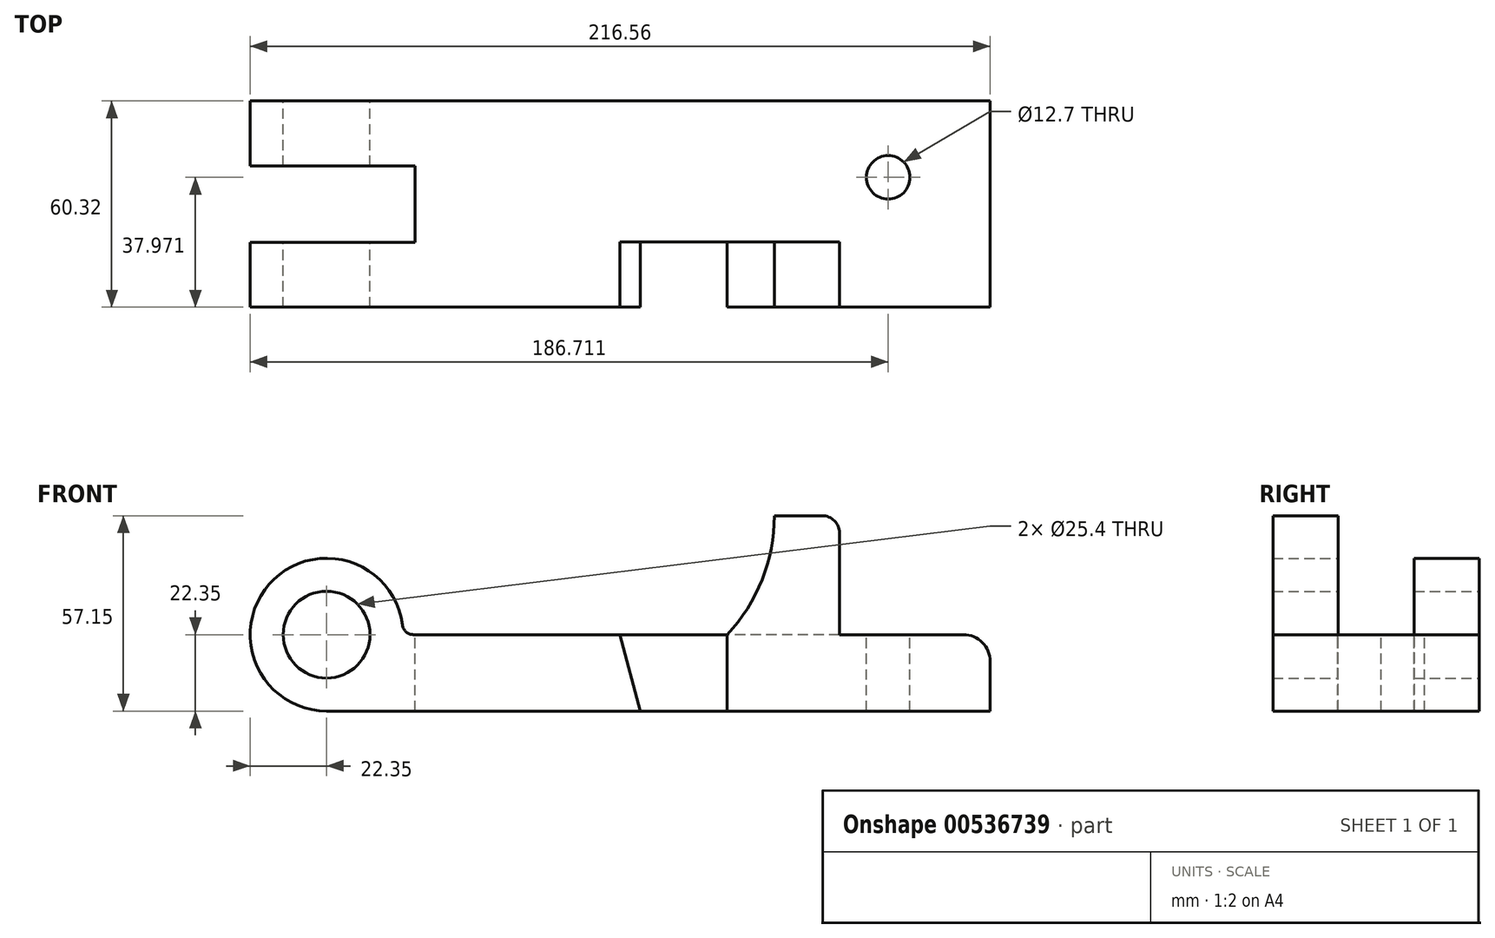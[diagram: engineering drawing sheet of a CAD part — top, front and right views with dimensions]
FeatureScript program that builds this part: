
annotation { "Feature Type Name" : "Feature", "Feature Type Description" : "" }
export const myFeature = defineFeature(function(context is Context, id is Id, definition is map)
    precondition{}
    {
        {
            var Q0;
            Q0=qCreatedBy(makeId("Front.planeOp"),FACE);
            var sketch = newSketch(context, id + "F0", { "sketchPlane" : qUnion([Q0])});
            skCircle(sketch, "E0", {"center": v(0, 0) * mm, "radius": 12.7 * mm});
            skCircle(sketch, "E1", {"center": v(0, 0) * mm, "radius": 22.35 * mm});
            skLineSegment(sketch, "E2.bottom", {"start": v(0, -22.35) * mm, "end": v(194.2, -22.35) * mm});
            skLineSegment(sketch, "E2.top", {"start": v(22.35, 0) * mm, "end": v(194.2, 0) * mm});
            skLineSegment(sketch, "E2.right", {"start": v(194.2, -22.35) * mm, "end": v(194.2, 0) * mm});
            skSolve(sketch);
        }
        {
            var Q0;
            {var subQ0=sQuery(id+"F0.wireOp",EDGE,"E2.bottom");Q0=makeQuery(id+"F0.imprint","IMPRINT",FACE,{"disambiguationData":[TD([[makeQuery(id+"F0.imprint","IMPRINT",EDGE,{"derivedFrom":subQ0}),1.0]])]});}
            var Q1;
            Q1=makeQuery(id+"F0.imprint","IMPRINT",FACE,{"disambiguationData":[TD([[makeQuery(id+"F0.imprint","IMPRINT",EDGE,{"derivedFrom":sQuery(id+"F0.wireOp",EDGE,"E0")}),-1.0]])]});
            extrude(context, id + "F1", {"entities" : qUnion([Q0, Q1]), "endBound" : BoundingType.SYMMETRIC, "depth" : 60.32 * mm, "offsetDistance" : 25.4 * mm});
        }
        {
            var Q0;
            Q0=qCreatedBy(makeId("Top.planeOp"),FACE);
            var sketch = newSketch(context, id + "F2", { "sketchPlane" : qUnion([Q0])});
            skLineSegment(sketch, "E3", {"start": v(-22.35, -30.16) * mm, "end": v(-22.35, 30.16) * mm});
            skLineSegment(sketch, "E4.bottom", {"start": v(-22.35, 11.16) * mm, "end": v(25.9, 11.16) * mm});
            skLineSegment(sketch, "E4.top", {"start": v(-22.35, -11.16) * mm, "end": v(25.9, -11.16) * mm});
            skLineSegment(sketch, "E4.left", {"start": v(-22.35, 11.16) * mm, "end": v(-22.35, -11.16) * mm});
            skLineSegment(sketch, "E4.right", {"start": v(25.9, 11.16) * mm, "end": v(25.9, -11.16) * mm});
            skPoint(sketch, "E4.middle", {"position": v(1.78, 0) * mm});
            skSolve(sketch);
        }
        {
            var Q0;
            Q0=makeQuery(id+"F2.imprint","IMPRINT",FACE,{"disambiguationData":[TD([[makeQuery(id+"F2.imprint","IMPRINT",EDGE,{"derivedFrom":sQuery(id+"F2.wireOp",EDGE,"E4.bottom")}),-1.0]])]});
            extrude(context, id + "F3", {"entities" : qUnion([Q0]), "operationType" : NewBodyOperationType.REMOVE, "endBound" : BoundingType.SYMMETRIC, "oppositeDirection" : true, "depth" : .88 * 50.8 * mm, "offsetDistance" : 25.4 * mm});
        }
        {
            var Q0;
            Q0=makeQuery(id+"F1.opExtrude","CAP_FACE",FACE,{"disambiguationData":[OSD([sQuery(id+"F0.wireOp",EDGE,"E0"),sQuery(id+"F0.wireOp",EDGE,"E1"),sQuery(id+"F0.wireOp",EDGE,"E2.bottom"),sQuery(id+"F0.wireOp",EDGE,"E2.top"),sQuery(id+"F0.wireOp",EDGE,"E2.right")])],"isStart":false});
            var sketch = newSketch(context, id + "F4", { "sketchPlane" : qUnion([Q0])});
            skLineSegment(sketch, "E5", {"start": v(91.85, -22.35) * mm, "end": v(117.25, -22.35) * mm});
            skLineSegment(sketch, "E6", {"start": v(117.25, -22.35) * mm, "end": v(117.25, 0) * mm});
            skLineSegment(sketch, "E7", {"start": v(117.25, 0) * mm, "end": v(85.85, 0) * mm});
            skLineSegment(sketch, "E8", {"start": v(85.85, 0) * mm, "end": v(91.85, -22.35) * mm});
            skSolve(sketch);
        }
        {
            var Q0;
            Q0=makeQuery(id+"F4.imprint","IMPRINT",FACE,{"disambiguationData":[TD([[makeQuery(id+"F4.imprint","IMPRINT",EDGE,{"derivedFrom":sQuery(id+"F4.wireOp",EDGE,"E5")}),1.0]])]});
            extrude(context, id + "F5", {"entities" : qUnion([Q0]), "operationType" : NewBodyOperationType.REMOVE, "oppositeDirection" : true, "depth" : 19.05 * mm, "offsetDistance" : 25.4 * mm});
        }
        {
            var Q0;
            {var subQ0=sQuery(id+"F0.wireOp",EDGE,"E2.bottom");var subQ1=sQuery(id+"F0.wireOp",EDGE,"E2.top");var subQ2=sQuery(id+"F0.wireOp",EDGE,"E2.right");Q0=makeQuery(id+"F5.boolean.opBoolean","SPLIT",FACE,{"disambiguationData":[TD([makeQuery(id+"F1.opExtrude","SWEPT_FACE",FACE,{"disambiguationData":[OSD([subQ2])]})])],"derivedFrom":makeQuery(id+"F1.opExtrude","CAP_FACE",FACE,{"disambiguationData":[OSD([sQuery(id+"F0.wireOp",EDGE,"E0"),sQuery(id+"F0.wireOp",EDGE,"E1"),subQ0,subQ1,subQ2])],"isStart":false})});}
            var sketch = newSketch(context, id + "F6", { "sketchPlane" : qUnion([Q0])});
            skLineSegment(sketch, "E9", {"start": v(150.09, 0) * mm, "end": v(150.09, 34.8) * mm});
            skLineSegment(sketch, "E10", {"start": v(150.09, 34.8) * mm, "end": v(131.04, 34.8) * mm});
            skArc(sketch, "E11", {"start": v(117.25, 0) * mm, "mid": v(127.46, 16.08) * mm, "end": v(131.04, 34.8) * mm});
            skSolve(sketch);
        }
        {
            var Q0;
            Q0 = qSketchRegion(id + "F6", true);
            var Q1;
            {var subQ0=sQuery(id+"F6.wireOp",EDGE,"E9");Q1=makeQuery(id+"F6.imprint","IMPRINT",FACE,{"disambiguationData":[TD([[makeQuery(id+"F6.imprint","IMPRINT",EDGE,{"derivedFrom":subQ0}),1.0]])]});}
            var Q2;
            Q2=makeQuery(id+"F5.boolean.opBoolean","COPY",FACE,{"derivedFrom":makeQuery(id+"F5.opExtrude","CAP_FACE",FACE,{"disambiguationData":[OSD([sQuery(id+"F4.wireOp",EDGE,"E5"),sQuery(id+"F4.wireOp",EDGE,"E6"),sQuery(id+"F4.wireOp",EDGE,"E7"),sQuery(id+"F4.wireOp",EDGE,"E8")])],"isStart":false})});
            extrude(context, id + "F7", {"entities" : qUnion([Q0, Q1]), "operationType" : NewBodyOperationType.ADD, "endBound" : BoundingType.UP_TO_SURFACE, "oppositeDirection" : true, "depth" : 25.4 * mm, "endBoundEntityFace" : qUnion([Q2]), "offsetDistance" : 25.4 * mm});
        }
        {
            var Q0;
            Q0=makeQuery(id+"F1.opExtrude","SWEPT_FACE",FACE,{"disambiguationData":[OSD([sQuery(id+"F0.wireOp",EDGE,"E2.top")])]});
            var sketch = newSketch(context, id + "F8", { "sketchPlane" : qUnion([Q0])});
            skCircle(sketch, "E12", {"center": v(164.36, 7.81) * mm, "radius": 6.35 * mm});
            skSolve(sketch);
        }
        {
            var Q0;
            Q0=makeQuery(id+"F8.imprint","IMPRINT",FACE,{"disambiguationData":[TD([[makeQuery(id+"F8.imprint","IMPRINT",EDGE,{"derivedFrom":sQuery(id+"F8.wireOp",EDGE,"E12")}),1.0]])]});
            extrude(context, id + "F9", {"entities" : qUnion([Q0]), "operationType" : NewBodyOperationType.REMOVE, "endBound" : BoundingType.THROUGH_ALL, "oppositeDirection" : true, "depth" : 25.4 * mm, "offsetDistance" : 25.4 * mm});
        }
        {
            var Q0;
            {var subQ0=sQuery(id+"F0.wireOp",EDGE,"E2.top");var subQ1=sQuery(id+"F0.wireOp",EDGE,"E1");Q0=makeQuery(id+"F3.boolean.opBoolean","SPLIT",EDGE,{"disambiguationData":[TD([makeQuery(id+"F3.opExtrude","SWEPT_FACE",FACE,{"disambiguationData":[OSD([sQuery(id+"F2.wireOp",EDGE,"E4.top")])]})])],"derivedFrom":makeQuery(id+"F1.opExtrude","SWEPT_EDGE",EDGE,{"disambiguationData":[OSD([subQ1,subQ0])]})});}
            var Q1;
            Q1=makeQuery(id+"F7.opExtrude","SWEPT_EDGE",EDGE,{"disambiguationData":[OSD([sQuery(id+"F0.wireOp",EDGE,"E2.top"),sQuery(id+"F6.wireOp",EDGE,"E9")])]});
            var Q2;
            {var subQ0=sQuery(id+"F0.wireOp",EDGE,"E2.top");var subQ1=sQuery(id+"F0.wireOp",EDGE,"E1");Q2=makeQuery(id+"F3.boolean.opBoolean","SPLIT",EDGE,{"disambiguationData":[TD([makeQuery(id+"F3.opExtrude","SWEPT_FACE",FACE,{"disambiguationData":[OSD([sQuery(id+"F2.wireOp",EDGE,"E4.bottom")])]})])],"derivedFrom":makeQuery(id+"F1.opExtrude","SWEPT_EDGE",EDGE,{"disambiguationData":[OSD([subQ1,subQ0])]})});}
            fillet(context, id + "F10", {"entities" : qUnion([Q0, Q1, Q2]), "radius" : 3.3 * mm, "tangentPropagation" : true, "allowEdgeOverflow" : false});
        }
        {
            var Q0;
            Q0=makeQuery(id+"F1.opExtrude","SWEPT_EDGE",EDGE,{"disambiguationData":[OSD([sQuery(id+"F0.wireOp",EDGE,"E2.top"),sQuery(id+"F0.wireOp",EDGE,"E2.right")])]});
            fillet(context, id + "F11", {"entities" : qUnion([Q0]), "radius" : 7.87 * mm, "tangentPropagation" : true, "allowEdgeOverflow" : false});
        }
        {
            var Q0;
            Q0=makeQuery(id+"F7.opExtrude","SWEPT_EDGE",EDGE,{"disambiguationData":[OSD([sQuery(id+"F6.wireOp",EDGE,"E9"),sQuery(id+"F6.wireOp",EDGE,"E10")])]});
            fillet(context, id + "F12", {"entities" : qUnion([Q0]), "radius" : 5.08 * mm, "tangentPropagation" : true, "allowEdgeOverflow" : false});
        }
    });
